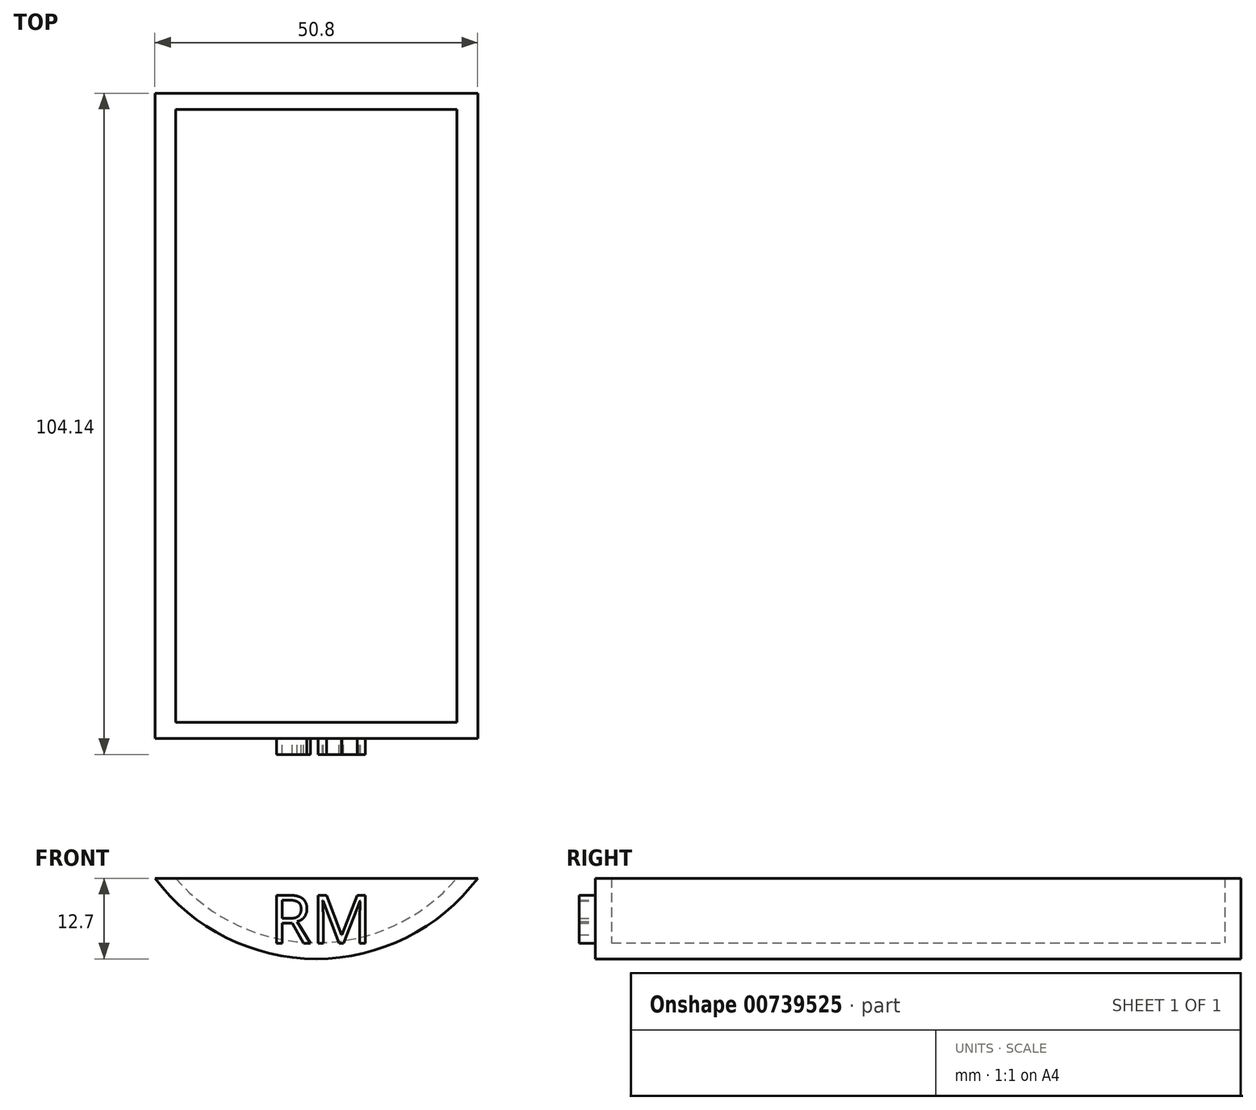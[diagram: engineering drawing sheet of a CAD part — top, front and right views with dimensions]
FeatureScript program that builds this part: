
annotation { "Feature Type Name" : "Feature", "Feature Type Description" : "" }
export const myFeature = defineFeature(function(context is Context, id is Id, definition is map)
    precondition{}
    {
        {
            var Q0;
            Q0=qCreatedBy(makeId("Front.planeOp"),FACE);
            var sketch = newSketch(context, id + "F0", { "sketchPlane" : qUnion([Q0])});
            skLineSegment(sketch, "E0", {"start": v(-50.08, 39.27) * mm, "end": v(0.72, 39.27) * mm});
            skLineSegment(sketch, "E1", {"start": v(-24.68, 39.27) * mm, "end": v(-24.68, 26.57) * mm});
            skArc(sketch, "E2", {"start": v(-50.08, 39.27) * mm, "mid": v(-24.68, 26.57) * mm, "end": v(0.72, 39.27) * mm});
            skSolve(sketch);
        }
        {
            var Q0;
            {var subQ3=sQuery(id+"F0.wireOp",EDGE,"E1");Q0=makeQuery(id+"F0.imprint","IMPRINT",FACE,{"disambiguationData":[TD([[makeQuery(id+"F0.imprint","IMPRINT",EDGE,{"derivedFrom":subQ3}),1.0]])]});}
            var Q1;
            {var subQ3=sQuery(id+"F0.wireOp",EDGE,"E1");Q1=makeQuery(id+"F0.imprint","IMPRINT",FACE,{"disambiguationData":[TD([[makeQuery(id+"F0.imprint","IMPRINT",EDGE,{"derivedFrom":subQ3}),-1.0]])]});}
            extrude(context, id + "F1", {"entities" : qUnion([Q0, Q1]), "depth" : 101.6 * mm, "offsetDistance" : 25.4 * mm});
        }
        {
            var Q0;
            Q0=makeQuery(id+"F1.opExtrude","SWEPT_FACE",FACE,{"disambiguationData":[OSD([sQuery(id+"F0.wireOp",EDGE,"E0")])]});
            shell(context, id + "F2", {"entities" : qUnion([Q0]), "thickness" : 2.54 * mm});
        }
        {
            var Q0;
            Q0=makeQuery(id+"F1.opExtrude","CAP_FACE",FACE,{"disambiguationData":[OSD([sQuery(id+"F0.wireOp",EDGE,"E0"),sQuery(id+"F0.wireOp",EDGE,"E2")])],"isStart":false});
            var sketch = newSketch(context, id + "F3", { "sketchPlane" : qUnion([Q0])});
            skText(sketch, "E3", { "text": "RM", "fontName": "OpenSans-Regular.ttf"});
            const initialGuessF3  = {"E3": [-0.03197, 0.02905, 1, 0, 0.0076]};
            skSetInitialGuess(sketch, initialGuessF3);
            skSolve(sketch);
        }
        {
            var Q0;
            Q0 = qSketchRegion(id + "F3", true);
            extrude(context, id + "F4", {"entities" : qUnion([Q0]), "operationType" : NewBodyOperationType.ADD, "depth" : 2.54 * mm, "offsetDistance" : 25.4 * mm});
        }
    });
